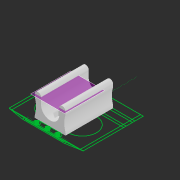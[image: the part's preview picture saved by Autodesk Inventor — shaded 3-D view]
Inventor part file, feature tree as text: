
AUTODESK INVENTOR PART (.ipt)
format: ipt  version: 2020.3 (Build 243373010, 373A)  size: 346,624 bytes
history: native  units: mm
features: fillet x7, extrude x5, sketch x2, other x1, plane x1, projected_geometry x1
ambient origin geometry x8: Origin, YZ Plane, XZ Plane, XY Plane, X Axis, Y Axis, Z Axis, Center Point
bodies: Solid1 (feature_tree)
feature tree (17):
  other  "body.ipt"
  extrude  "Extrusion1"  Depth=10.0mm
  extrude  "Extrusion2"  Depth=6.0mm
  sketch  "Sketch3"  dims[d2=22.0mm d3=5.8mm d4=5.8mm d5=4.0mm d6=0.0mm d7=15.0mm d8=0.0mm d9=6.0mm d10=6.0mm d11=34.062mm d12=0.0mm d13=2.3mm d14=2.3mm d15=2.0mm d16=2.0mm d18=-15.25mm d19=14.25mm d20=0.0mm d21=0.4mm d22=0.2mm d23=2.0mm d24=0.8mm d25=17.0mm d26=2.0mm d27=2.0mm d28=34.063mm d29=0.0mm d30=6.0mm]
  extrude  "Extrusion3"  Depth=6.0mm
  fillet  "Fillet1"  Radius=4.0mm
  fillet  "Fillet2"  Radius=15.0mm
  plane  "Work Plane1"
  extrude  "Extrusion4"  Depth=6.0mm
  fillet  "Fillet4"  Radius=6.0mm
  fillet  "Fillet5"  Radius=34.062mm
  fillet  "Fillet6"  Radius=2.3mm
  fillet  "Fillet7"  Radius=2.3mm
  extrude  "Extrusion5"  Depth=6.0mm
  fillet  "Fillet8"  Radius=2.0mm
  sketch  "Sketch1"  dims[d0=10.0mm d1=13.0mm]
  projected_geometry  "Projected Loop1"
